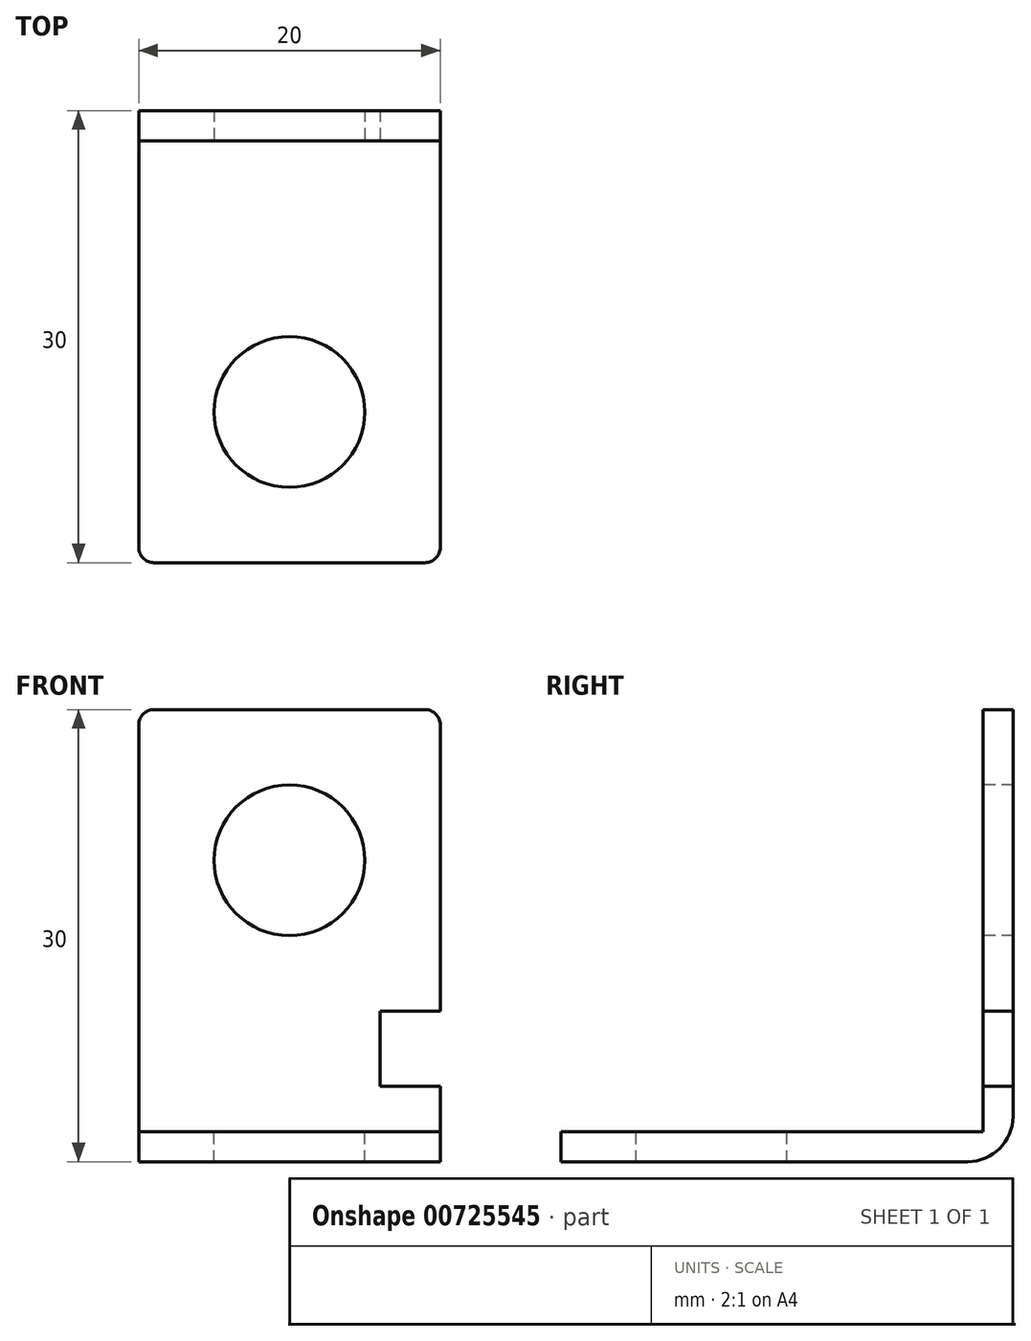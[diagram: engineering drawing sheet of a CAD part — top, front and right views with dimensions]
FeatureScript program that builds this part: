
annotation { "Feature Type Name" : "Feature", "Feature Type Description" : "" }
export const myFeature = defineFeature(function(context is Context, id is Id, definition is map)
    precondition{}
    {
        {
            var Q0;
            Q0=qCreatedBy(makeId("Top.planeOp"),FACE);
            var sketch = newSketch(context, id + "F0", { "sketchPlane" : qUnion([Q0])});
            skLineSegment(sketch, "E0.bottom", {"start": v(10, -15) * mm, "end": v(-10, -15) * mm});
            skLineSegment(sketch, "E0.top", {"start": v(10, 15) * mm, "end": v(-10, 15) * mm});
            skLineSegment(sketch, "E0.left", {"start": v(10, -15) * mm, "end": v(10, 15) * mm});
            skLineSegment(sketch, "E0.right", {"start": v(-10, -15) * mm, "end": v(-10, 15) * mm});
            skPoint(sketch, "E0.middle", {"position": v(0, 0) * mm});
            skSolve(sketch);
        }
        {
            var Q0;
            Q0=makeQuery(id+"F0.imprint","IMPRINT",FACE,{"disambiguationData":[TD([[makeQuery(id+"F0.imprint","IMPRINT",EDGE,{"derivedFrom":sQuery(id+"F0.wireOp",EDGE,"E0.bottom")}),-1.0]])]});
            extrude(context, id + "F1", {"entities" : qUnion([Q0]), "depth" : 2 * mm, "offsetDistance" : 25 * mm});
        }
        {
            var Q0;
            Q0=makeQuery(id+"F1.opExtrude","CAP_FACE",FACE,{"disambiguationData":[OSD([sQuery(id+"F0.wireOp",EDGE,"E0.bottom"),sQuery(id+"F0.wireOp",EDGE,"E0.top"),sQuery(id+"F0.wireOp",EDGE,"E0.left"),sQuery(id+"F0.wireOp",EDGE,"E0.right")])],"isStart":false});
            var sketch = newSketch(context, id + "F2", { "sketchPlane" : qUnion([Q0])});
            skLineSegment(sketch, "E1.bottom", {"start": v(-10, 15) * mm, "end": v(10, 15) * mm});
            skLineSegment(sketch, "E1.top", {"start": v(-10, 13) * mm, "end": v(10, 13) * mm});
            skLineSegment(sketch, "E1.left", {"start": v(-10, 15) * mm, "end": v(-10, 13) * mm});
            skLineSegment(sketch, "E1.right", {"start": v(10, 15) * mm, "end": v(10, 13) * mm});
            skSolve(sketch);
        }
        {
            var Q0;
            Q0=makeQuery(id+"F2.imprint","IMPRINT",FACE,{"disambiguationData":[TD([[makeQuery(id+"F2.imprint","IMPRINT",EDGE,{"derivedFrom":sQuery(id+"F2.wireOp",EDGE,"E1.bottom")}),1.0]])]});
            extrude(context, id + "F3", {"entities" : qUnion([Q0]), "operationType" : NewBodyOperationType.ADD, "depth" : 28 * mm, "offsetDistance" : 25 * mm});
        }
        {
            var Q0;
            Q0=makeQuery(id+"F1.opExtrude","CAP_EDGE",EDGE,{"disambiguationData":[OSD([sQuery(id+"F0.wireOp",EDGE,"E0.top")])],"isStart":true});
            fillet(context, id + "F4", {"entities" : qUnion([Q0]), "radius" : 3 * mm, "tangentPropagation" : true, "allowEdgeOverflow" : false});
        }
        {
            var Q0;
            Q0=makeQuery(id+"F1.opExtrude","SWEPT_EDGE",EDGE,{"disambiguationData":[OSD([sQuery(id+"F0.wireOp",EDGE,"E0.bottom"),sQuery(id+"F0.wireOp",EDGE,"E0.left")])]});
            var Q1;
            Q1=makeQuery(id+"F1.opExtrude","SWEPT_EDGE",EDGE,{"disambiguationData":[OSD([sQuery(id+"F0.wireOp",EDGE,"E0.bottom"),sQuery(id+"F0.wireOp",EDGE,"E0.right")])]});
            var Q2;
            Q2=makeQuery(id+"F3.opExtrude","CAP_EDGE",EDGE,{"disambiguationData":[OSD([sQuery(id+"F2.wireOp",EDGE,"E1.right")])],"isStart":false});
            var Q3;
            Q3=makeQuery(id+"F3.opExtrude","CAP_EDGE",EDGE,{"disambiguationData":[OSD([sQuery(id+"F2.wireOp",EDGE,"E1.left")])],"isStart":false});
            var Q4;
            Q4=makeQuery(id+"F3.opExtrude","CAP_EDGE",EDGE,{"disambiguationData":[OSD([sQuery(id+"F2.wireOp",EDGE,"E1.top")])],"isStart":true});
            fillet(context, id + "F5", {"entities" : qUnion([Q0, Q1, Q2, Q3, Q4]), "radius" : 1 * mm, "tangentPropagation" : true, "allowEdgeOverflow" : false});
        }
        {
            var Q0;
            Q0=makeQuery(id+"F1.opExtrude","CAP_FACE",FACE,{"disambiguationData":[OSD([sQuery(id+"F0.wireOp",EDGE,"E0.bottom"),sQuery(id+"F0.wireOp",EDGE,"E0.top"),sQuery(id+"F0.wireOp",EDGE,"E0.left"),sQuery(id+"F0.wireOp",EDGE,"E0.right")])],"isStart":false});
            var sketch = newSketch(context, id + "F6", { "sketchPlane" : qUnion([Q0])});
            skCircle(sketch, "E2", {"center": v(0, -5) * mm, "radius": 5 * mm});
            skSolve(sketch);
        }
        {
            var Q0;
            Q0 = qSketchRegion(id + "F6", true);
            extrude(context, id + "F7", {"entities" : qUnion([Q0]), "operationType" : NewBodyOperationType.REMOVE, "endBound" : BoundingType.UP_TO_NEXT, "oppositeDirection" : true, "depth" : 25 * mm, "offsetDistance" : 25 * mm});
        }
        {
            var Q0;
            Q0=makeQuery(id+"F3.opExtrude","SWEPT_FACE",FACE,{"disambiguationData":[OSD([sQuery(id+"F2.wireOp",EDGE,"E1.top")])]});
            var sketch = newSketch(context, id + "F8", { "sketchPlane" : qUnion([Q0])});
            skCircle(sketch, "E3", {"center": v(0, 20) * mm, "radius": 5 * mm});
            skSolve(sketch);
        }
        {
            var Q0;
            Q0 = qSketchRegion(id + "F8", true);
            extrude(context, id + "F9", {"entities" : qUnion([Q0]), "operationType" : NewBodyOperationType.REMOVE, "endBound" : BoundingType.UP_TO_NEXT, "oppositeDirection" : true, "depth" : 25 * mm, "offsetDistance" : 25 * mm});
        }
        {
            var Q0;
            Q0=makeQuery(id+"F3.opExtrude","SWEPT_FACE",FACE,{"disambiguationData":[OSD([sQuery(id+"F2.wireOp",EDGE,"E1.top")])]});
            var sketch = newSketch(context, id + "F10", { "sketchPlane" : qUnion([Q0])});
            skLineSegment(sketch, "E4.bottom", {"start": v(10, 10) * mm, "end": v(6, 10) * mm});
            skLineSegment(sketch, "E4.top", {"start": v(10, 5) * mm, "end": v(6, 5) * mm});
            skLineSegment(sketch, "E4.left", {"start": v(10, 10) * mm, "end": v(10, 5) * mm});
            skLineSegment(sketch, "E4.right", {"start": v(6, 10) * mm, "end": v(6, 5) * mm});
            skSolve(sketch);
        }
        {
            var Q0;
            Q0=makeQuery(id+"F10.imprint","IMPRINT",FACE,{"disambiguationData":[TD([[makeQuery(id+"F10.imprint","IMPRINT",EDGE,{"derivedFrom":sQuery(id+"F10.wireOp",EDGE,"E4.bottom")}),1.0]])]});
            extrude(context, id + "F11", {"entities" : qUnion([Q0]), "operationType" : NewBodyOperationType.REMOVE, "endBound" : BoundingType.UP_TO_NEXT, "oppositeDirection" : true, "depth" : 25 * mm, "offsetDistance" : 25 * mm});
        }
    });
